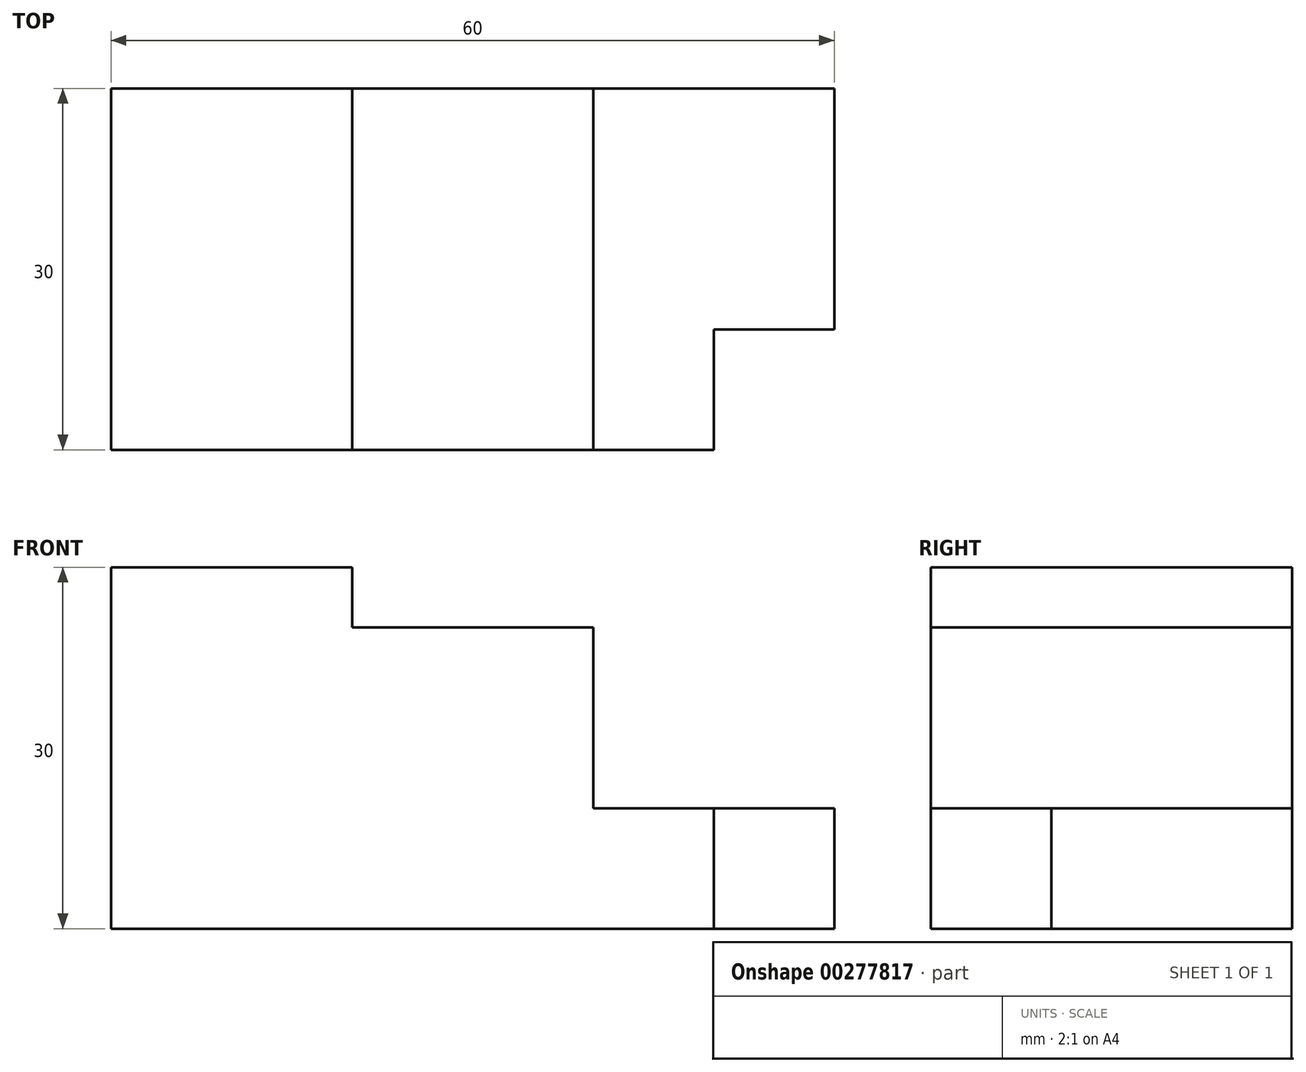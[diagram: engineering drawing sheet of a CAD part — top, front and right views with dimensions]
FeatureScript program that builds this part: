
annotation { "Feature Type Name" : "Feature", "Feature Type Description" : "" }
export const myFeature = defineFeature(function(context is Context, id is Id, definition is map)
    precondition{}
    {
        {
            var Q0;
            Q0=qCreatedBy(makeId("Front.planeOp"),FACE);
            var sketch = newSketch(context, id + "F0", { "sketchPlane" : qUnion([Q0])});
            skLineSegment(sketch, "E0", {"start": v(0, 0) * mm, "end": v(0, 30) * mm});
            skLineSegment(sketch, "E1", {"start": v(0, 30) * mm, "end": v(20, 30) * mm});
            skLineSegment(sketch, "E2", {"start": v(20, 30) * mm, "end": v(20, 25) * mm});
            skLineSegment(sketch, "E3", {"start": v(20, 25) * mm, "end": v(40, 25) * mm});
            skLineSegment(sketch, "E4", {"start": v(40, 25) * mm, "end": v(40, 10) * mm});
            skLineSegment(sketch, "E5", {"start": v(40, 10) * mm, "end": v(60, 10) * mm});
            skLineSegment(sketch, "E6", {"start": v(0, 0) * mm, "end": v(60, 0) * mm});
            skLineSegment(sketch, "E7", {"start": v(60, 0) * mm, "end": v(60, 10) * mm});
            skLineSegment(sketch, "E8", {"start": v(50, 10) * mm, "end": v(50, 0) * mm});
            skSolve(sketch);
        }
        {
            var Q0;
            {var subQ1=sQuery(id+"F0.wireOp",EDGE,"E0");Q0=makeQuery(id+"F0.imprint","IMPRINT",FACE,{"disambiguationData":[TD([[makeQuery(id+"F0.imprint","IMPRINT",EDGE,{"derivedFrom":subQ1}),-1.0]])]});}
            var Q1;
            {var subQ0=sQuery(id+"F0.wireOp",EDGE,"E7");Q1=makeQuery(id+"F0.imprint","IMPRINT",FACE,{"disambiguationData":[TD([[makeQuery(id+"F0.imprint","IMPRINT",EDGE,{"derivedFrom":subQ0}),1.0]])]});}
            extrude(context, id + "F1", {"entities" : qUnion([Q0, Q1]), "oppositeDirection" : true, "depth" : 30 * mm});
        }
        {
            var Q0;
            {var subQ0=sQuery(id+"F0.wireOp",EDGE,"E7");Q0=makeQuery(id+"F0.imprint","IMPRINT",FACE,{"disambiguationData":[TD([[makeQuery(id+"F0.imprint","IMPRINT",EDGE,{"derivedFrom":subQ0}),1.0]])]});}
            extrude(context, id + "F2", {"entities" : qUnion([Q0]), "operationType" : NewBodyOperationType.REMOVE, "oppositeDirection" : true, "depth" : 10 * mm});
        }
    });
